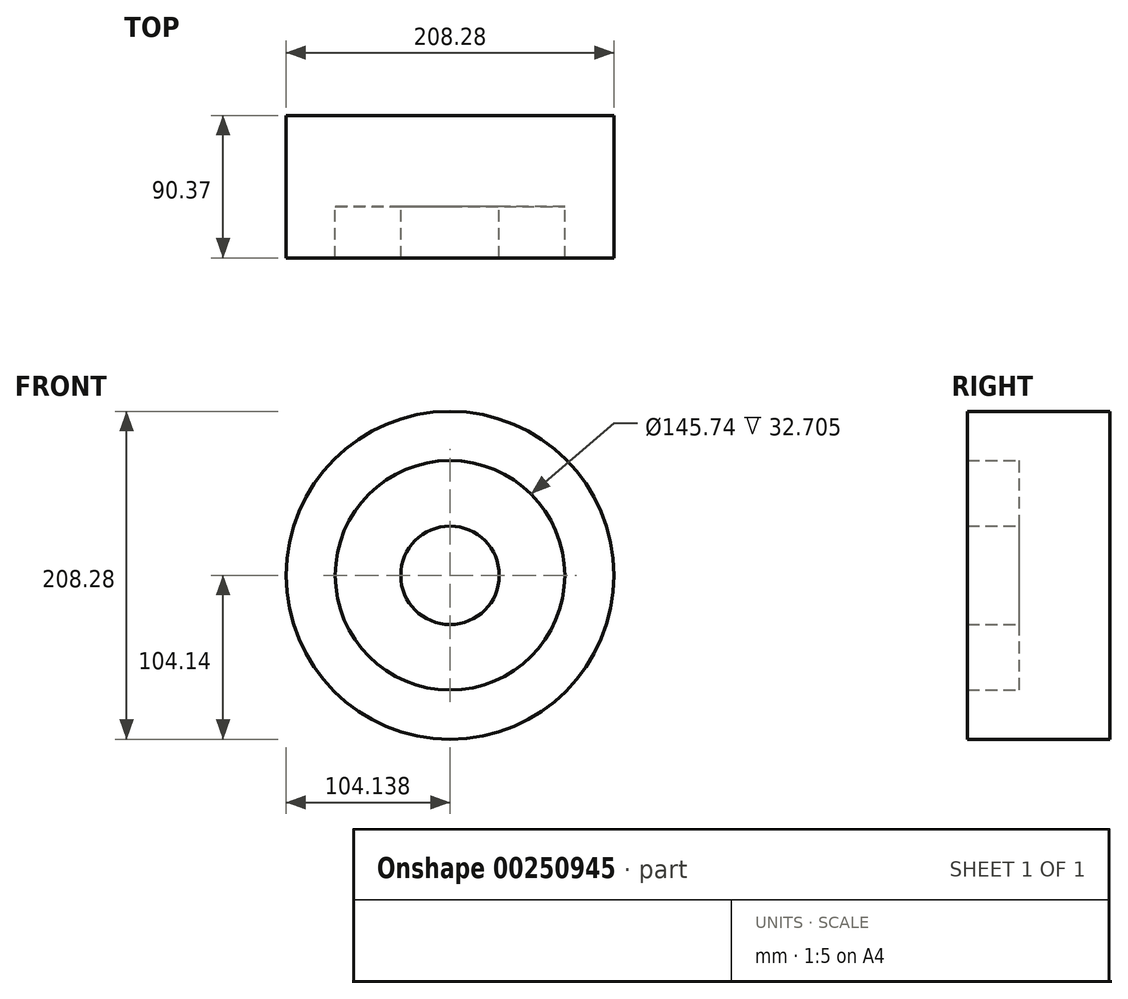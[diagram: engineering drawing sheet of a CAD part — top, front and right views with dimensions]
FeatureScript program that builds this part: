
annotation { "Feature Type Name" : "Feature", "Feature Type Description" : "" }
export const myFeature = defineFeature(function(context is Context, id is Id, definition is map)
    precondition{}
    {
        {
            var Q0;
            Q0=qCreatedBy(makeId("Top.planeOp"),FACE);
            var sketch = newSketch(context, id + "F0", { "sketchPlane" : qUnion([Q0])});
            skLineSegment(sketch, "E0", {"start": v(-55.08, 39.16) * mm, "end": v(-55.08, -51.2) * mm});
            skLineSegment(sketch, "E1", {"start": v(-55.08, -51.2) * mm, "end": v(-23.81, -51.2) * mm});
            skLineSegment(sketch, "E2", {"start": v(-23.81, -51.2) * mm, "end": v(-23.81, -18.5) * mm});
            skLineSegment(sketch, "E3", {"start": v(-23.81, -18.5) * mm, "end": v(17.79, -18.5) * mm});
            skLineSegment(sketch, "E4", {"start": v(17.79, -18.5) * mm, "end": v(17.79, -51.2) * mm});
            skLineSegment(sketch, "E5", {"start": v(17.79, -51.2) * mm, "end": v(49.06, -51.2) * mm});
            skLineSegment(sketch, "E6", {"start": v(49.06, -51.2) * mm, "end": v(49.06, 40.02) * mm});
            skLineSegment(sketch, "E7", {"start": v(-55.08, 39.16) * mm, "end": v(49.06, 39.16) * mm});
            skPoint(sketch, "E8", {"position": v(0, 0) * mm});
            skSolve(sketch);
        }
        {
            var Q0;
            Q0=makeQuery(id+"F0.imprint","IMPRINT",FACE,{"disambiguationData":[TD([[makeQuery(id+"F0.imprint","IMPRINT",EDGE,{"derivedFrom":sQuery(id+"F0.wireOp",EDGE,"E0")}),1.0]])]});
            var Q1;
            Q1=sQuery(id+"F0.wireOp",EDGE,"E0");
            revolve(context, id + "F1", {"entities" : qUnion([Q0]), "axis" : qUnion([Q1]), "revolveType" : RevolveType.FULL});
        }
    });
